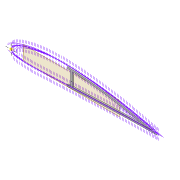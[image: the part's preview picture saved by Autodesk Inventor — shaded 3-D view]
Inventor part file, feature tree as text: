
AUTODESK INVENTOR PART (.ipt)
format: ipt  version: 2022 (Build 260153000, 153)  size: 361,984 bytes
history: native  units: mm
features: extrude x7, sketch x7, projected_geometry x5, shell x1, fillet x1, plane x1
ambient origin geometry x8: Origin, YZ Plane, XZ Plane, XY Plane, X Axis, Y Axis, Z Axis, Center Point
bodies: Solid1 (feature_tree)
feature tree (22):
  extrude  "Extrusion1"  Depth=5.0mm
  shell  "Shell1"  Thickness=2.0mm
  extrude  "Extrusion8"  Depth=5.9mm
  extrude  "Extrusion3"  Depth=10.0mm TaperAngle=0.0deg
  extrude  "Extrusion4"  Depth=2.0mm
  fillet  "Fillet1"  Radius=5.0mm
  extrude  "Extrusion5"  Depth=2.5mm
  plane  "Work Plane2"
  extrude  "Extrusion9"  Depth=1.6mm
  extrude  "Extrusion10"  Depth=75.0mm
  sketch  "Sketch3"  dims[d0=4.0mm d1=0.0mm d2=5.0mm d7=2.0mm]
  sketch  "Sketch8"  dims[d8=2.0mm d9=5.9mm]
  sketch  "Sketch9"  dims[d13=10.0mm d14=0.0mm d16=10.0mm d17=0.0mm]
  sketch  "Sketch10"  dims[d22=4.0mm d23=0.0mm d31=2.0mm d32=5.0mm]
  projected_geometry  "Projected Loop4"
  projected_geometry  "Projected Loop10"
  sketch  "Sketch24"  dims[d34=1.6mm d35=2.5mm]
  projected_geometry  "Projected Loop11"
  projected_geometry  "Projected Loop12"
  sketch  "Sketch26"  dims[d37=5.0mm d38=1.6mm]
  projected_geometry  "Projected Loop13"
  sketch  "Sketch27"  dims[d40=2.5mm d62=75.0mm d63=6.0mm d64=4.0mm d65=0.0mm d66=3.0mm d67=12.0mm d68=75.0mm d69=20.0mm d70=0.5mm d71=10.0mm d72=0.0mm d73=10.0mm d74=0.0mm]
